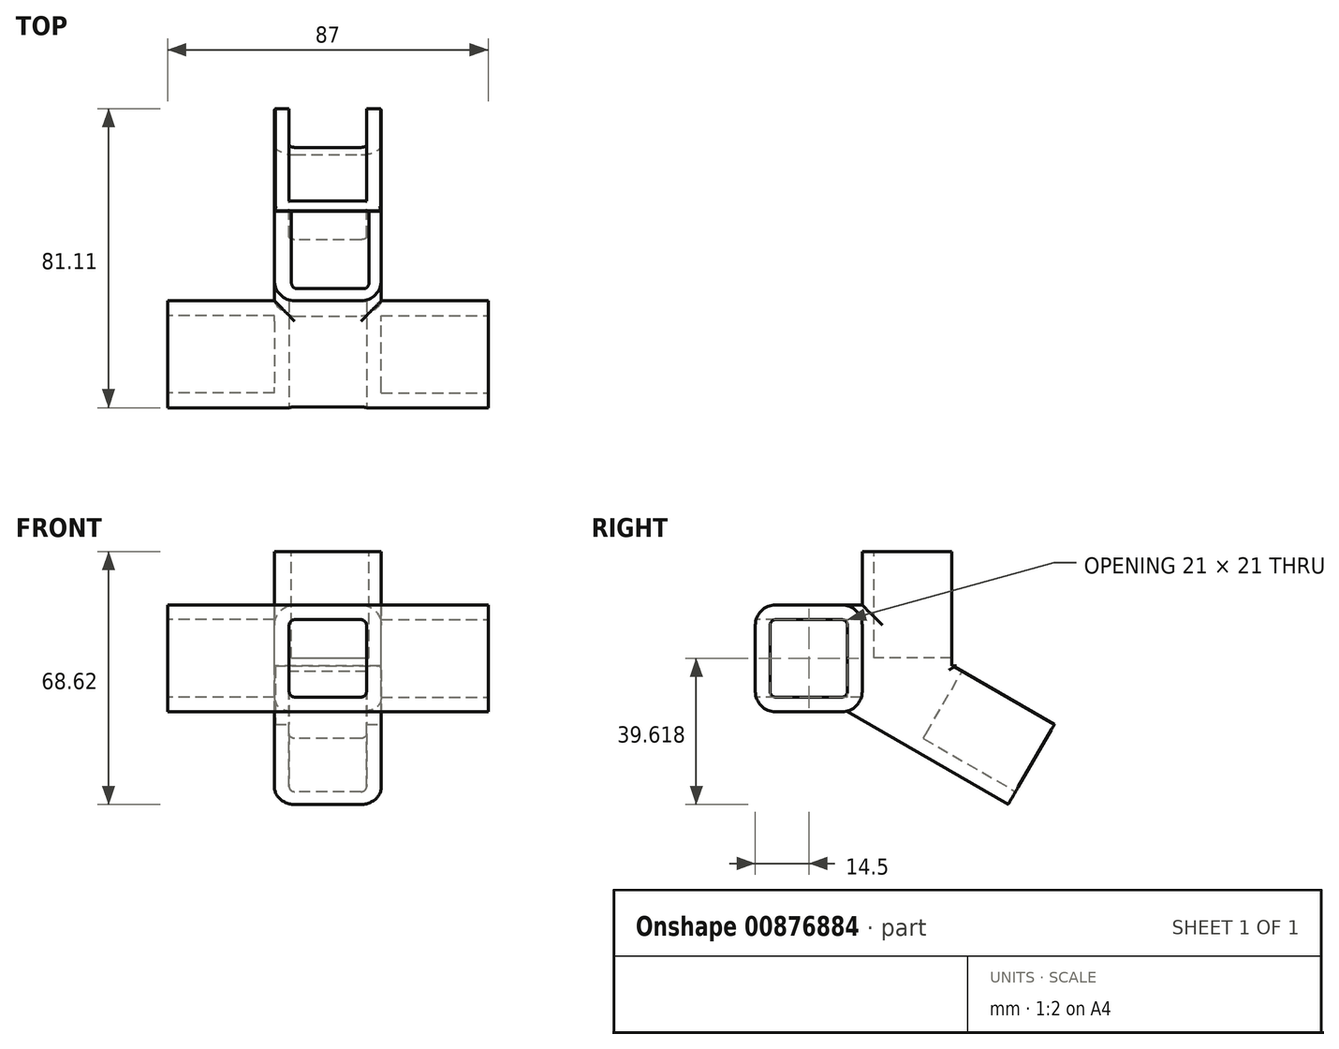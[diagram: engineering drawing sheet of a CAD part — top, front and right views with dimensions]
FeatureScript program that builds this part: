
annotation { "Feature Type Name" : "Feature", "Feature Type Description" : "" }
export const myFeature = defineFeature(function(context is Context, id is Id, definition is map)
    precondition{}
    {
        {
            var Q0;
            Q0=qCreatedBy(makeId("Front.planeOp"),FACE);
            var sketch = newSketch(context, id + "F0", { "sketchPlane" : qUnion([Q0])});
            skLineSegment(sketch, "E0.bottom", {"start": v(-40.9, 10.25) * mm, "end": v(46.1, 10.25) * mm});
            skLineSegment(sketch, "E0.top", {"start": v(-40.9, -18.75) * mm, "end": v(46.1, -18.75) * mm});
            skLineSegment(sketch, "E0.left", {"start": v(-40.9, 10.25) * mm, "end": v(-40.9, -18.75) * mm});
            skLineSegment(sketch, "E0.right", {"start": v(46.1, 10.25) * mm, "end": v(46.1, -18.75) * mm});
            skSolve(sketch);
        }
        {
            var Q0;
            Q0=makeQuery(id+"F0.imprint","IMPRINT",FACE,{"disambiguationData":[TD([[makeQuery(id+"F0.imprint","IMPRINT",EDGE,{"derivedFrom":sQuery(id+"F0.wireOp",EDGE,"E0.bottom")}),-1.0]])]});
            extrude(context, id + "F1", {"entities" : qUnion([Q0]), "depth" : 29 * mm, "offsetDistance" : 25 * mm});
        }
        {
            var Q0;
            Q0=makeQuery(id+"F1.opExtrude","CAP_FACE",FACE,{"disambiguationData":[OSD([sQuery(id+"F0.wireOp",EDGE,"E0.bottom"),sQuery(id+"F0.wireOp",EDGE,"E0.top"),sQuery(id+"F0.wireOp",EDGE,"E0.left"),sQuery(id+"F0.wireOp",EDGE,"E0.right")])],"isStart":false});
            var sketch = newSketch(context, id + "F2", { "sketchPlane" : qUnion([Q0])});
            skLineSegment(sketch, "E1.bottom", {"start": v(-7.9, 6.25) * mm, "end": v(13.1, 6.25) * mm});
            skLineSegment(sketch, "E1.top", {"start": v(-7.9, -14.75) * mm, "end": v(13.1, -14.75) * mm});
            skLineSegment(sketch, "E1.left", {"start": v(-7.9, 6.25) * mm, "end": v(-7.9, -14.75) * mm});
            skLineSegment(sketch, "E1.right", {"start": v(13.1, 6.25) * mm, "end": v(13.1, -14.75) * mm});
            skSolve(sketch);
        }
        {
            var Q0;
            Q0=makeQuery(id+"F2.imprint","IMPRINT",FACE,{"disambiguationData":[TD([[makeQuery(id+"F2.imprint","IMPRINT",EDGE,{"derivedFrom":sQuery(id+"F2.wireOp",EDGE,"E1.bottom")}),-1.0]])]});
            extrude(context, id + "F3", {"entities" : qUnion([Q0]), "operationType" : NewBodyOperationType.REMOVE, "oppositeDirection" : true, "depth" : 28.9 * mm, "offsetDistance" : 25 * mm});
        }
        {
            var Q0;
            Q0=makeQuery(id+"F1.opExtrude","SWEPT_FACE",FACE,{"disambiguationData":[OSD([sQuery(id+"F0.wireOp",EDGE,"E0.right")])]});
            var sketch = newSketch(context, id + "F4", { "sketchPlane" : qUnion([Q0])});
            skLineSegment(sketch, "E2.bottom", {"start": v(-25, 6.25) * mm, "end": v(-4, 6.25) * mm});
            skLineSegment(sketch, "E2.top", {"start": v(-25, -14.75) * mm, "end": v(-4, -14.75) * mm});
            skLineSegment(sketch, "E2.left", {"start": v(-25, 6.25) * mm, "end": v(-25, -14.75) * mm});
            skLineSegment(sketch, "E2.right", {"start": v(-4, 6.25) * mm, "end": v(-4, -14.75) * mm});
            skSolve(sketch);
        }
        {
            var Q0;
            Q0=makeQuery(id+"F4.imprint","IMPRINT",FACE,{"disambiguationData":[TD([[makeQuery(id+"F4.imprint","IMPRINT",EDGE,{"derivedFrom":sQuery(id+"F4.wireOp",EDGE,"E2.bottom")}),-1.0]])]});
            extrude(context, id + "F5", {"entities" : qUnion([Q0]), "operationType" : NewBodyOperationType.REMOVE, "oppositeDirection" : true, "depth" : 29 * mm, "offsetDistance" : 25 * mm});
        }
        {
            var Q0;
            Q0=makeQuery(id+"F1.opExtrude","SWEPT_FACE",FACE,{"disambiguationData":[OSD([sQuery(id+"F0.wireOp",EDGE,"E0.left")])]});
            var sketch = newSketch(context, id + "F6", { "sketchPlane" : qUnion([Q0])});
            skLineSegment(sketch, "E3.bottom", {"start": v(4, 6.25) * mm, "end": v(25, 6.25) * mm});
            skLineSegment(sketch, "E3.top", {"start": v(4, -14.75) * mm, "end": v(25, -14.75) * mm});
            skLineSegment(sketch, "E3.left", {"start": v(4, 6.25) * mm, "end": v(4, -14.75) * mm});
            skLineSegment(sketch, "E3.right", {"start": v(25, 6.25) * mm, "end": v(25, -14.75) * mm});
            skSolve(sketch);
        }
        {
            var Q0;
            Q0=makeQuery(id+"F6.imprint","IMPRINT",FACE,{"disambiguationData":[TD([[makeQuery(id+"F6.imprint","IMPRINT",EDGE,{"derivedFrom":sQuery(id+"F6.wireOp",EDGE,"E3.bottom")}),-1.0]])]});
            extrude(context, id + "F7", {"entities" : qUnion([Q0]), "operationType" : NewBodyOperationType.REMOVE, "oppositeDirection" : true, "depth" : 29 * mm, "offsetDistance" : 25 * mm});
        }
        {
            var Q0;
            Q0=makeQuery(id+"F1.opExtrude","SWEPT_FACE",FACE,{"disambiguationData":[OSD([sQuery(id+"F0.wireOp",EDGE,"E0.bottom")])]});
            var sketch = newSketch(context, id + "F8", { "sketchPlane" : qUnion([Q0])});
            skLineSegment(sketch, "E4.bottom", {"start": v(-11.9, 0) * mm, "end": v(17.1, 0) * mm});
            skLineSegment(sketch, "E4.top", {"start": v(-11.9, 29) * mm, "end": v(17.1, 29) * mm});
            skLineSegment(sketch, "E4.left", {"start": v(-11.9, 0) * mm, "end": v(-11.9, 29) * mm});
            skLineSegment(sketch, "E4.right", {"start": v(17.1, 0) * mm, "end": v(17.1, 29) * mm});
            skSolve(sketch);
        }
        {
            var Q0;
            Q0=makeQuery(id+"F8.imprint","IMPRINT",FACE,{"disambiguationData":[TD([[makeQuery(id+"F8.imprint","IMPRINT",EDGE,{"derivedFrom":sQuery(id+"F8.wireOp",EDGE,"E4.bottom")}),1.0]])]});
            extrude(context, id + "F9", {"entities" : qUnion([Q0]), "operationType" : NewBodyOperationType.ADD, "oppositeDirection" : true, "depth" : 14.5 * mm, "offsetDistance" : 25 * mm});
        }
        {
            var Q0;
            Q0=makeQuery(id+"F9.boolean.opBoolean","MERGE",FACE,{"derivedFrom":[makeQuery(id+"F1.opExtrude","SWEPT_FACE",FACE,{"disambiguationData":[OSD([sQuery(id+"F0.wireOp",EDGE,"E0.bottom")])]}),makeQuery(id+"F9.opExtrude","CAP_FACE",FACE,{"disambiguationData":[OSD([sQuery(id+"F8.wireOp",EDGE,"E4.bottom"),sQuery(id+"F8.wireOp",EDGE,"E4.top"),sQuery(id+"F8.wireOp",EDGE,"E4.left"),sQuery(id+"F8.wireOp",EDGE,"E4.right")])],"isStart":true})]});
            var sketch = newSketch(context, id + "F10", { "sketchPlane" : qUnion([Q0])});
            skLineSegment(sketch, "E5.bottom", {"start": v(-11.9, 29) * mm, "end": v(17.1, 29) * mm});
            skLineSegment(sketch, "E5.top", {"start": v(-11.9, 0) * mm, "end": v(17.1, 0) * mm});
            skLineSegment(sketch, "E5.left", {"start": v(-11.9, 29) * mm, "end": v(-11.9, 0) * mm});
            skLineSegment(sketch, "E5.right", {"start": v(17.1, 29) * mm, "end": v(17.1, 0) * mm});
            skSolve(sketch);
        }
        {
            var Q0;
            Q0=makeQuery(id+"F10.imprint","IMPRINT",FACE,{"disambiguationData":[TD([[makeQuery(id+"F10.imprint","IMPRINT",EDGE,{"derivedFrom":sQuery(id+"F10.wireOp",EDGE,"E5.bottom")}),-1.0]])]});
            extrude(context, id + "F11", {"entities" : qUnion([Q0]), "operationType" : NewBodyOperationType.ADD, "depth" : 14.5 * mm, "offsetDistance" : 25 * mm});
        }
        {
            var Q0;
            Q0=makeQuery(id+"F11.opExtrude","CAP_FACE",FACE,{"disambiguationData":[OSD([sQuery(id+"F10.wireOp",EDGE,"E5.bottom"),sQuery(id+"F10.wireOp",EDGE,"E5.top"),sQuery(id+"F10.wireOp",EDGE,"E5.left"),sQuery(id+"F10.wireOp",EDGE,"E5.right")])],"isStart":false});
            var sketch = newSketch(context, id + "F12", { "sketchPlane" : qUnion([Q0])});
            skLineSegment(sketch, "E6.bottom", {"start": v(-7.27, 24.27) * mm, "end": v(13.73, 24.27) * mm});
            skLineSegment(sketch, "E6.top", {"start": v(-7.27, 3.27) * mm, "end": v(13.73, 3.27) * mm});
            skLineSegment(sketch, "E6.left", {"start": v(-7.27, 24.27) * mm, "end": v(-7.27, 3.27) * mm});
            skLineSegment(sketch, "E6.right", {"start": v(13.73, 24.27) * mm, "end": v(13.73, 3.27) * mm});
            skSolve(sketch);
        }
        {
            var Q0;
            Q0=makeQuery(id+"F12.imprint","IMPRINT",FACE,{"disambiguationData":[TD([[makeQuery(id+"F12.imprint","IMPRINT",EDGE,{"derivedFrom":sQuery(id+"F12.wireOp",EDGE,"E6.bottom")}),-1.0]])]});
            extrude(context, id + "F13", {"entities" : qUnion([Q0]), "operationType" : NewBodyOperationType.REMOVE, "oppositeDirection" : true, "depth" : 28.9 * mm, "offsetDistance" : 25 * mm});
        }
        {
            var Q0;
            Q0=makeQuery(id+"F11.boolean.opBoolean","MERGE",FACE,{"derivedFrom":[makeQuery(id+"F9.opExtrude","SWEPT_FACE",FACE,{"disambiguationData":[OSD([sQuery(id+"F8.wireOp",EDGE,"E4.right")])]}),makeQuery(id+"F11.opExtrude","SWEPT_FACE",FACE,{"disambiguationData":[OSD([sQuery(id+"F10.wireOp",EDGE,"E5.right")])]})]});
            var sketch = newSketch(context, id + "F14", { "sketchPlane" : qUnion([Q0])});
            skLineSegment(sketch, "E7", {"start": v(29, -4.25) * mm, "end": v(54.11, -18.75) * mm});
            skLineSegment(sketch, "E8", {"start": v(54.11, -18.75) * mm, "end": v(39.61, -43.87) * mm});
            skLineSegment(sketch, "E9", {"start": v(29, -4.25) * mm, "end": v(14.5, -29.37) * mm});
            skLineSegment(sketch, "E10", {"start": v(39.61, -43.87) * mm, "end": v(14.5, -29.37) * mm});
            skLineSegment(sketch, "E11", {"start": v(0, -18.75) * mm, "end": v(0, -4.25) * mm});
            skLineSegment(sketch, "E12", {"start": v(0, -4.25) * mm, "end": v(29, -4.25) * mm});
            skLineSegment(sketch, "E13", {"start": v(14.5, -29.37) * mm, "end": v(-4.37, -18.47) * mm});
            skLineSegment(sketch, "E14", {"start": v(-4.37, -18.47) * mm, "end": v(0, -18.75) * mm});
            skSolve(sketch);
        }
        {
            var Q0;
            Q0=makeQuery(id+"F14.imprint","IMPRINT",FACE,{"disambiguationData":[TD([[makeQuery(id+"F14.imprint","IMPRINT",EDGE,{"derivedFrom":sQuery(id+"F14.wireOp",EDGE,"E7")}),-1.0]])]});
            var Q1;
            Q1=makeQuery(id+"F14.imprint","IMPRINT",FACE,{"disambiguationData":[TD([[makeQuery(id+"F14.imprint","IMPRINT",EDGE,{"derivedFrom":sQuery(id+"F14.wireOp",EDGE,"E9")}),-1.0]])]});
            extrude(context, id + "F15", {"entities" : qUnion([Q0, Q1]), "operationType" : NewBodyOperationType.ADD, "oppositeDirection" : true, "depth" : 29 * mm, "offsetDistance" : 25 * mm});
        }
        {
            var Q0;
            Q0=makeQuery(id+"F15.opExtrude","SWEPT_FACE",FACE,{"disambiguationData":[OSD([sQuery(id+"F14.wireOp",EDGE,"E8")])]});
            var sketch = newSketch(context, id + "F16", { "sketchPlane" : qUnion([Q0])});
            skLineSegment(sketch, "E15.bottom", {"start": v(-13.1, -14.18) * mm, "end": v(7.9, -14.18) * mm});
            skLineSegment(sketch, "E15.top", {"start": v(-13.1, 6.82) * mm, "end": v(7.9, 6.82) * mm});
            skLineSegment(sketch, "E15.left", {"start": v(-13.1, -14.18) * mm, "end": v(-13.1, 6.82) * mm});
            skLineSegment(sketch, "E15.right", {"start": v(7.9, -14.18) * mm, "end": v(7.9, 6.82) * mm});
            skSolve(sketch);
        }
        {
            var Q0;
            Q0=makeQuery(id+"F16.imprint","IMPRINT",FACE,{"disambiguationData":[TD([[makeQuery(id+"F16.imprint","IMPRINT",EDGE,{"derivedFrom":sQuery(id+"F16.wireOp",EDGE,"E15.bottom")}),1.0]])]});
            extrude(context, id + "F17", {"entities" : qUnion([Q0]), "operationType" : NewBodyOperationType.REMOVE, "oppositeDirection" : true, "depth" : 28.9 * mm, "offsetDistance" : 25 * mm});
        }
        {
            var Q0;
            {var subQ1=sQuery(id+"F0.wireOp",EDGE,"E0.right");var subQ2=sQuery(id+"F0.wireOp",EDGE,"E0.top");Q0=makeQuery(id+"F15.boolean.opBoolean","SPLIT",EDGE,{"disambiguationData":[TD([makeQuery(id+"F1.opExtrude","SWEPT_FACE",FACE,{"disambiguationData":[OSD([subQ1])]})])],"derivedFrom":makeQuery(id+"F1.opExtrude","CAP_EDGE",EDGE,{"disambiguationData":[OSD([subQ2])],"isStart":true})});}
            var Q1;
            {var subQ1=sQuery(id+"F0.wireOp",EDGE,"E0.right");var subQ2=sQuery(id+"F0.wireOp",EDGE,"E0.bottom");Q1=makeQuery(id+"F9.boolean.opBoolean","SPLIT",EDGE,{"disambiguationData":[TD([makeQuery(id+"F1.opExtrude","SWEPT_FACE",FACE,{"disambiguationData":[OSD([subQ1])]})])],"derivedFrom":makeQuery(id+"F1.opExtrude","CAP_EDGE",EDGE,{"disambiguationData":[OSD([subQ2])],"isStart":true})});}
            var Q2;
            Q2=makeQuery(id+"F11.boolean.opBoolean","MERGE",EDGE,{"derivedFrom":[makeQuery(id+"F9.opExtrude","SWEPT_EDGE",EDGE,{"disambiguationData":[OSD([sQuery(id+"F8.wireOp",EDGE,"E4.top"),sQuery(id+"F8.wireOp",EDGE,"E4.right")])]}),makeQuery(id+"F11.opExtrude","SWEPT_EDGE",EDGE,{"disambiguationData":[OSD([sQuery(id+"F10.wireOp",EDGE,"E5.bottom"),sQuery(id+"F10.wireOp",EDGE,"E5.right")])]})]});
            var Q3;
            Q3=makeQuery(id+"F15.opExtrude","CAP_EDGE",EDGE,{"disambiguationData":[OSD([sQuery(id+"F14.wireOp",EDGE,"E7")])],"isStart":true});
            var Q4;
            Q4=makeQuery(id+"F15.opExtrude","CAP_EDGE",EDGE,{"disambiguationData":[OSD([sQuery(id+"F14.wireOp",EDGE,"E10")])],"isStart":true});
            var Q5;
            Q5=makeQuery(id+"F15.opExtrude","CAP_EDGE",EDGE,{"disambiguationData":[OSD([sQuery(id+"F14.wireOp",EDGE,"rhXE65Le-xGBt-KA5q-W1Vl-ZSKlkg2fR1oH")])],"isStart":true});
            fillet(context, id + "F18", {"entities" : qUnion([Q0, Q1, Q2, Q3, Q4, Q5]), "radius" : 5.5 * mm, "tangentPropagation" : true, "allowEdgeOverflow" : false});
        }
        {
            var Q0;
            Q0=makeQuery(id+"F15.opExtrude","CAP_EDGE",EDGE,{"disambiguationData":[OSD([sQuery(id+"F14.wireOp",EDGE,"E7")])],"isStart":false});
            var Q1;
            Q1=makeQuery(id+"F15.opExtrude","CAP_EDGE",EDGE,{"disambiguationData":[OSD([sQuery(id+"F14.wireOp",EDGE,"E10")])],"isStart":false});
            var Q2;
            Q2=makeQuery(id+"F15.opExtrude","CAP_EDGE",EDGE,{"disambiguationData":[OSD([sQuery(id+"F14.wireOp",EDGE,"rhXE65Le-xGBt-KA5q-W1Vl-ZSKlkg2fR1oH")])],"isStart":false});
            var Q3;
            Q3=makeQuery(id+"F11.boolean.opBoolean","MERGE",EDGE,{"derivedFrom":[makeQuery(id+"F9.opExtrude","SWEPT_EDGE",EDGE,{"disambiguationData":[OSD([sQuery(id+"F8.wireOp",EDGE,"E4.top"),sQuery(id+"F8.wireOp",EDGE,"E4.left")])]}),makeQuery(id+"F11.opExtrude","SWEPT_EDGE",EDGE,{"disambiguationData":[OSD([sQuery(id+"F10.wireOp",EDGE,"E5.bottom"),sQuery(id+"F10.wireOp",EDGE,"E5.left")])]})]});
            var Q4;
            {var subQ0=sQuery(id+"F0.wireOp",EDGE,"E0.left");var subQ2=sQuery(id+"F0.wireOp",EDGE,"E0.bottom");Q4=makeQuery(id+"F9.boolean.opBoolean","SPLIT",EDGE,{"disambiguationData":[TD([makeQuery(id+"F1.opExtrude","SWEPT_FACE",FACE,{"disambiguationData":[OSD([subQ0])]})])],"derivedFrom":makeQuery(id+"F1.opExtrude","CAP_EDGE",EDGE,{"disambiguationData":[OSD([subQ2])],"isStart":true})});}
            var Q5;
            Q5=makeQuery(id+"F1.opExtrude","CAP_EDGE",EDGE,{"disambiguationData":[OSD([sQuery(id+"F0.wireOp",EDGE,"E0.top")])],"isStart":false});
            var Q6;
            Q6=makeQuery(id+"F1.opExtrude","CAP_EDGE",EDGE,{"disambiguationData":[OSD([sQuery(id+"F0.wireOp",EDGE,"E0.bottom")])],"isStart":false});
            fillet(context, id + "F19", {"entities" : qUnion([Q0, Q1, Q2, Q3, Q4, Q5, Q6]), "radius" : 5.5 * mm, "tangentPropagation" : true, "allowEdgeOverflow" : false});
        }
        {
            var Q0;
            Q0=makeQuery(id+"F11.opExtrude","SWEPT_EDGE",EDGE,{"disambiguationData":[OSD([sQuery(id+"F0.wireOp",EDGE,"E0.bottom"),sQuery(id+"F10.wireOp",EDGE,"E5.top"),sQuery(id+"F10.wireOp",EDGE,"E5.right")])]});
            var Q1;
            Q1=makeQuery(id+"F11.opExtrude","SWEPT_EDGE",EDGE,{"disambiguationData":[OSD([sQuery(id+"F0.wireOp",EDGE,"E0.bottom"),sQuery(id+"F10.wireOp",EDGE,"E5.top"),sQuery(id+"F10.wireOp",EDGE,"E5.left")])]});
            fillet(context, id + "F20", {"entities" : qUnion([Q0, Q1]), "radius" : 5.5 * mm, "tangentPropagation" : true, "allowEdgeOverflow" : false});
        }
        {
            var Q0;
            {var subQ0=sQuery(id+"F0.wireOp",EDGE,"E0.bottom");Q0=makeQuery(id+"F19.opFillet","TWEAK_EDGE",EDGE,{"derivedFrom":[makeQuery(id+"F11.boolean.opBoolean","MERGE",VERTEX,{"derivedFrom":[makeQuery(id+"F9.opExtrude","CAP_VERTEX",VERTEX,{"disambiguationData":[OSD([subQ0,sQuery(id+"F8.wireOp",EDGE,"E4.bottom"),sQuery(id+"F8.wireOp",EDGE,"E4.left")])],"isStart":true}),makeQuery(id+"F11.opExtrude","CAP_VERTEX",VERTEX,{"disambiguationData":[OSD([subQ0,sQuery(id+"F10.wireOp",EDGE,"E5.top"),sQuery(id+"F10.wireOp",EDGE,"E5.left")])],"isStart":true})]})]});}
            var Q1;
            {var subQ0=sQuery(id+"F0.wireOp",EDGE,"E0.bottom");Q1=makeQuery(id+"F18.opFillet","TWEAK_EDGE",EDGE,{"derivedFrom":[makeQuery(id+"F11.boolean.opBoolean","MERGE",VERTEX,{"derivedFrom":[makeQuery(id+"F9.opExtrude","CAP_VERTEX",VERTEX,{"disambiguationData":[OSD([subQ0,sQuery(id+"F8.wireOp",EDGE,"E4.bottom"),sQuery(id+"F8.wireOp",EDGE,"E4.right")])],"isStart":true}),makeQuery(id+"F11.opExtrude","CAP_VERTEX",VERTEX,{"disambiguationData":[OSD([subQ0,sQuery(id+"F10.wireOp",EDGE,"E5.top"),sQuery(id+"F10.wireOp",EDGE,"E5.right")])],"isStart":true})]})]});}
            fillet(context, id + "F21", {"entities" : qUnion([Q0, Q1]), "radius" : 5.5 * mm, "tangentPropagation" : true, "allowEdgeOverflow" : false});
        }
        {
            var Q0;
            Q0=makeQuery(id+"F5.boolean.opBoolean","COPY",EDGE,{"derivedFrom":makeQuery(id+"F5.opExtrude","SWEPT_EDGE",EDGE,{"disambiguationData":[OSD([sQuery(id+"F4.wireOp",EDGE,"E2.top"),sQuery(id+"F4.wireOp",EDGE,"E2.right")])]})});
            var Q1;
            Q1=makeQuery(id+"F5.boolean.opBoolean","COPY",EDGE,{"derivedFrom":makeQuery(id+"F5.opExtrude","SWEPT_EDGE",EDGE,{"disambiguationData":[OSD([sQuery(id+"F4.wireOp",EDGE,"E2.bottom"),sQuery(id+"F4.wireOp",EDGE,"E2.right")])]})});
            var Q2;
            Q2=makeQuery(id+"F5.boolean.opBoolean","COPY",EDGE,{"derivedFrom":makeQuery(id+"F5.opExtrude","SWEPT_EDGE",EDGE,{"disambiguationData":[OSD([sQuery(id+"F4.wireOp",EDGE,"E2.bottom"),sQuery(id+"F4.wireOp",EDGE,"E2.left")])]})});
            var Q3;
            Q3=makeQuery(id+"F5.boolean.opBoolean","COPY",EDGE,{"derivedFrom":makeQuery(id+"F5.opExtrude","SWEPT_EDGE",EDGE,{"disambiguationData":[OSD([sQuery(id+"F4.wireOp",EDGE,"E2.top"),sQuery(id+"F4.wireOp",EDGE,"E2.left")])]})});
            var Q4;
            Q4=makeQuery(id+"F3.boolean.opBoolean","COPY",EDGE,{"derivedFrom":makeQuery(id+"F3.opExtrude","SWEPT_EDGE",EDGE,{"disambiguationData":[OSD([sQuery(id+"F2.wireOp",EDGE,"E1.top"),sQuery(id+"F2.wireOp",EDGE,"E1.left")])]})});
            var Q5;
            Q5=makeQuery(id+"F3.boolean.opBoolean","COPY",EDGE,{"derivedFrom":makeQuery(id+"F3.opExtrude","SWEPT_EDGE",EDGE,{"disambiguationData":[OSD([sQuery(id+"F2.wireOp",EDGE,"E1.top"),sQuery(id+"F2.wireOp",EDGE,"E1.right")])]})});
            var Q6;
            Q6=makeQuery(id+"F3.boolean.opBoolean","COPY",EDGE,{"derivedFrom":makeQuery(id+"F3.opExtrude","SWEPT_EDGE",EDGE,{"disambiguationData":[OSD([sQuery(id+"F2.wireOp",EDGE,"E1.bottom"),sQuery(id+"F2.wireOp",EDGE,"E1.right")])]})});
            var Q7;
            Q7=makeQuery(id+"F3.boolean.opBoolean","COPY",EDGE,{"derivedFrom":makeQuery(id+"F3.opExtrude","SWEPT_EDGE",EDGE,{"disambiguationData":[OSD([sQuery(id+"F2.wireOp",EDGE,"E1.bottom"),sQuery(id+"F2.wireOp",EDGE,"E1.left")])]})});
            var Q8;
            Q8=makeQuery(id+"F7.boolean.opBoolean","COPY",EDGE,{"derivedFrom":makeQuery(id+"F7.opExtrude","SWEPT_EDGE",EDGE,{"disambiguationData":[OSD([sQuery(id+"F6.wireOp",EDGE,"E3.top"),sQuery(id+"F6.wireOp",EDGE,"E3.left")])]})});
            var Q9;
            Q9=makeQuery(id+"F7.boolean.opBoolean","COPY",EDGE,{"derivedFrom":makeQuery(id+"F7.opExtrude","SWEPT_EDGE",EDGE,{"disambiguationData":[OSD([sQuery(id+"F6.wireOp",EDGE,"E3.bottom"),sQuery(id+"F6.wireOp",EDGE,"E3.left")])]})});
            var Q10;
            Q10=makeQuery(id+"F7.boolean.opBoolean","COPY",EDGE,{"derivedFrom":makeQuery(id+"F7.opExtrude","SWEPT_EDGE",EDGE,{"disambiguationData":[OSD([sQuery(id+"F6.wireOp",EDGE,"E3.top"),sQuery(id+"F6.wireOp",EDGE,"E3.right")])]})});
            var Q11;
            Q11=makeQuery(id+"F7.boolean.opBoolean","COPY",EDGE,{"derivedFrom":makeQuery(id+"F7.opExtrude","SWEPT_EDGE",EDGE,{"disambiguationData":[OSD([sQuery(id+"F6.wireOp",EDGE,"E3.bottom"),sQuery(id+"F6.wireOp",EDGE,"E3.right")])]})});
            var Q12;
            Q12=makeQuery(id+"F17.boolean.opBoolean","COPY",EDGE,{"derivedFrom":makeQuery(id+"F17.opExtrude","SWEPT_EDGE",EDGE,{"disambiguationData":[OSD([sQuery(id+"F16.wireOp",EDGE,"E15.bottom"),sQuery(id+"F16.wireOp",EDGE,"E15.left")])]})});
            var Q13;
            Q13=makeQuery(id+"F17.boolean.opBoolean","COPY",EDGE,{"derivedFrom":makeQuery(id+"F17.opExtrude","SWEPT_EDGE",EDGE,{"disambiguationData":[OSD([sQuery(id+"F16.wireOp",EDGE,"E15.bottom"),sQuery(id+"F16.wireOp",EDGE,"E15.right")])]})});
            var Q14;
            Q14=makeQuery(id+"F13.boolean.opBoolean","COPY",EDGE,{"derivedFrom":makeQuery(id+"F13.opExtrude","SWEPT_EDGE",EDGE,{"disambiguationData":[OSD([sQuery(id+"F12.wireOp",EDGE,"E6.top"),sQuery(id+"F12.wireOp",EDGE,"E6.right")])]})});
            var Q15;
            Q15=makeQuery(id+"F13.boolean.opBoolean","COPY",EDGE,{"derivedFrom":makeQuery(id+"F13.opExtrude","SWEPT_EDGE",EDGE,{"disambiguationData":[OSD([sQuery(id+"F12.wireOp",EDGE,"E6.top"),sQuery(id+"F12.wireOp",EDGE,"E6.left")])]})});
            fillet(context, id + "F22", {"entities" : qUnion([Q0, Q1, Q2, Q3, Q4, Q5, Q6, Q7, Q8, Q9, Q10, Q11, Q12, Q13, Q14, Q15]), "radius" : 1.5 * mm, "tangentPropagation" : true, "allowEdgeOverflow" : false});
        }
        {
            var Q0;
            Q0=makeQuery(id+"F11.opExtrude","CAP_FACE",FACE,{"disambiguationData":[OSD([sQuery(id+"F10.wireOp",EDGE,"E5.bottom"),sQuery(id+"F10.wireOp",EDGE,"E5.top"),sQuery(id+"F10.wireOp",EDGE,"E5.left"),sQuery(id+"F10.wireOp",EDGE,"E5.right")])],"isStart":false});
            var sketch = newSketch(context, id + "F23", { "sketchPlane" : qUnion([Q0])});
            skLineSegment(sketch, "E16", {"start": v(-7.27, 24.27) * mm, "end": v(19.3, 24.27) * mm});
            skLineSegment(sketch, "E17", {"start": v(19.3, 24.27) * mm, "end": v(20.17, 31.04) * mm});
            skLineSegment(sketch, "E18", {"start": v(20.17, 31.04) * mm, "end": v(-17.17, 32.57) * mm});
            skLineSegment(sketch, "E19", {"start": v(-17.17, 32.57) * mm, "end": v(-17.17, 24.27) * mm});
            skLineSegment(sketch, "E20", {"start": v(-7.27, 24.27) * mm, "end": v(-17.17, 24.27) * mm});
            skSolve(sketch);
        }
        {
            var Q0;
            {var subQ0=sQuery(id+"F10.wireOp",EDGE,"E5.bottom");var subQ1=makeQuery(id+"F11.opExtrude","CAP_EDGE",EDGE,{"disambiguationData":[OSD([subQ0])],"isStart":false});Q0=makeQuery(id+"F23.imprint","IMPRINT",FACE,{"disambiguationData":[TD([[makeQuery(id+"F23.imprint","IMPRINT",EDGE,{"derivedFrom":subQ1}),-1.0]])]});}
            extrude(context, id + "F24", {"entities" : qUnion([Q0]), "operationType" : NewBodyOperationType.REMOVE, "oppositeDirection" : true, "depth" : 31 * mm, "offsetDistance" : 25 * mm});
        }
        {
            var Q0;
            Q0=makeQuery(id+"F15.opExtrude","SWEPT_FACE",FACE,{"disambiguationData":[OSD([sQuery(id+"F14.wireOp",EDGE,"E8")])]});
            var sketch = newSketch(context, id + "F25", { "sketchPlane" : qUnion([Q0])});
            skLineSegment(sketch, "E21.bottom", {"start": v(23.03, 24.68) * mm, "end": v(-28.87, 24.68) * mm});
            skLineSegment(sketch, "E21.top", {"start": v(23.03, 6.82) * mm, "end": v(-28.87, 6.82) * mm});
            skLineSegment(sketch, "E21.left", {"start": v(23.03, 24.68) * mm, "end": v(23.03, 6.82) * mm});
            skLineSegment(sketch, "E21.right", {"start": v(-28.87, 24.68) * mm, "end": v(-28.87, 6.82) * mm});
            skSolve(sketch);
        }
        {
            var Q0;
            {var subQ2=sQuery(id+"F14.wireOp",EDGE,"E8");var subQ4=sQuery(id+"F14.wireOp",EDGE,"E7");var subQ8=makeQuery(id+"F15.opExtrude","SWEPT_EDGE",EDGE,{"disambiguationData":[OSD([subQ4,subQ2])]});Q0=makeQuery(id+"F25.imprint","IMPRINT",FACE,{"disambiguationData":[TD([[makeQuery(id+"F25.imprint","IMPRINT",EDGE,{"derivedFrom":subQ8}),1.0]])]});}
            extrude(context, id + "F26", {"entities" : qUnion([Q0]), "operationType" : NewBodyOperationType.REMOVE, "oppositeDirection" : true, "depth" : 32 * mm, "offsetDistance" : 25 * mm});
        }
    });
